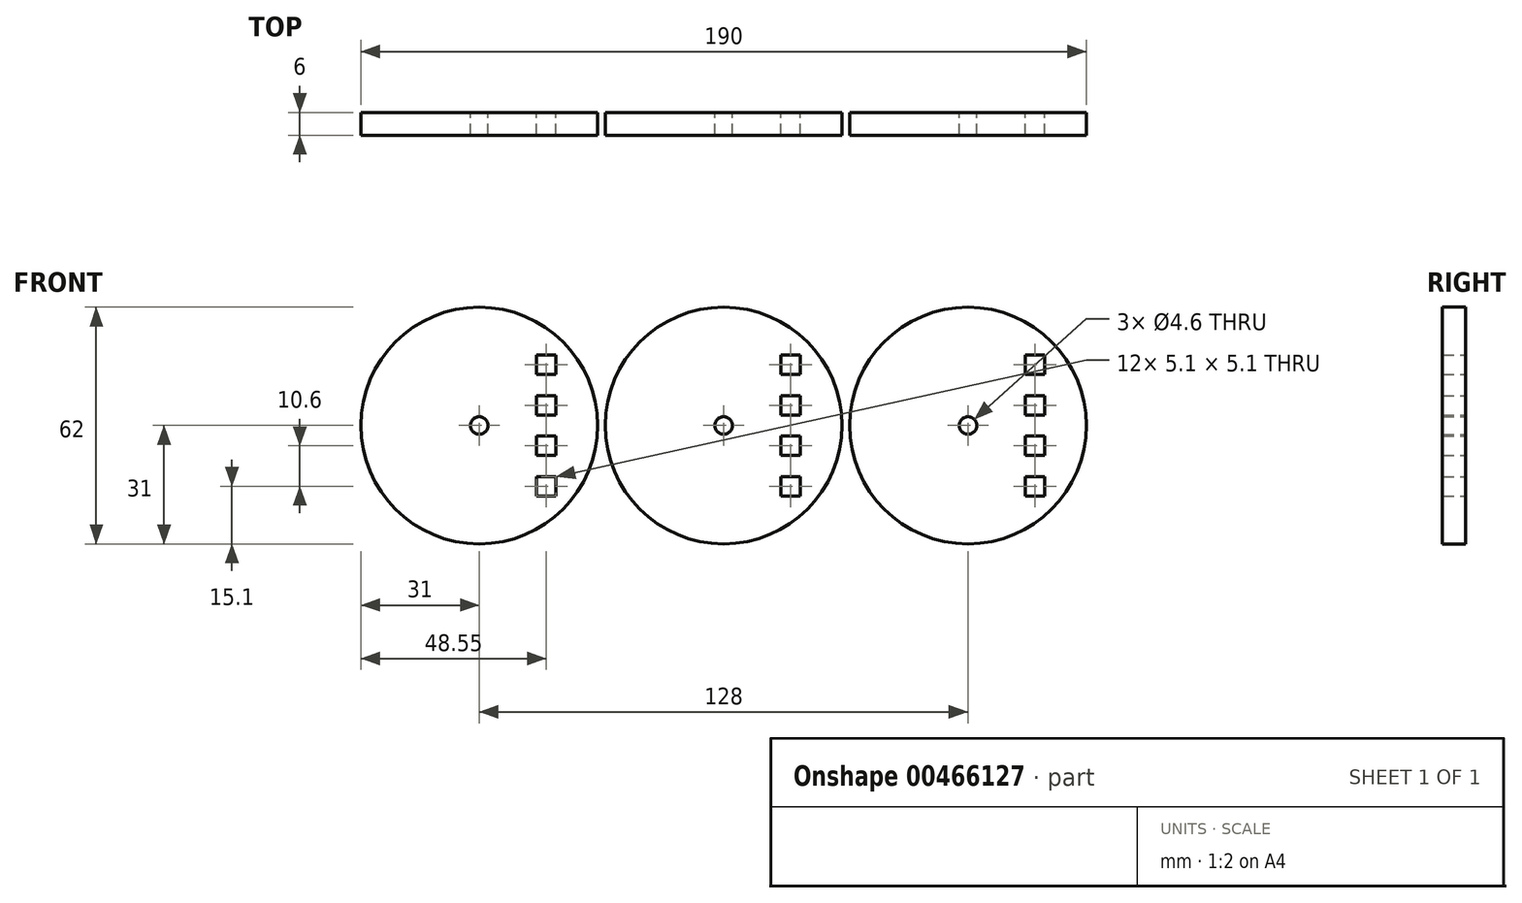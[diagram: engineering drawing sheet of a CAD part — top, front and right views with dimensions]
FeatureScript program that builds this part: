
annotation { "Feature Type Name" : "Feature", "Feature Type Description" : "" }
export const myFeature = defineFeature(function(context is Context, id is Id, definition is map)
    precondition{}
    {
        {
            var Q0;
            Q0=qCreatedBy(makeId("Front.planeOp"),FACE);
            var sketch = newSketch(context, id + "F0", { "sketchPlane" : qUnion([Q0])});
            skCircle(sketch, "E0", {"center": v(0, 0) * mm, "radius": 31 * mm});
            skLineSegment(sketch, "E1.bottom", {"start": v(15, 18.45) * mm, "end": v(20.1, 18.45) * mm});
            skLineSegment(sketch, "E1.top", {"start": v(15, 13.35) * mm, "end": v(20.1, 13.35) * mm});
            skLineSegment(sketch, "E1.left", {"start": v(15, 18.45) * mm, "end": v(15, 13.35) * mm});
            skLineSegment(sketch, "E1.right", {"start": v(20.1, 18.45) * mm, "end": v(20.1, 13.35) * mm});
            skLineSegment(sketch, "E2.bottom", {"start": v(15, 7.85) * mm, "end": v(20.1, 7.85) * mm});
            skLineSegment(sketch, "E2.top", {"start": v(15, 2.75) * mm, "end": v(20.1, 2.75) * mm});
            skLineSegment(sketch, "E2.left", {"start": v(15, 7.85) * mm, "end": v(15, 2.75) * mm});
            skLineSegment(sketch, "E2.right", {"start": v(20.1, 7.85) * mm, "end": v(20.1, 2.75) * mm});
            skLineSegment(sketch, "E3.bottom", {"start": v(15, -2.75) * mm, "end": v(20.1, -2.75) * mm});
            skLineSegment(sketch, "E3.top", {"start": v(15, -7.85) * mm, "end": v(20.1, -7.85) * mm});
            skLineSegment(sketch, "E3.left", {"start": v(15, -2.75) * mm, "end": v(15, -7.85) * mm});
            skLineSegment(sketch, "E3.right", {"start": v(20.1, -2.75) * mm, "end": v(20.1, -7.85) * mm});
            skLineSegment(sketch, "E4.bottom", {"start": v(15, -13.35) * mm, "end": v(20.1, -13.35) * mm});
            skLineSegment(sketch, "E4.top", {"start": v(15, -18.45) * mm, "end": v(20.1, -18.45) * mm});
            skLineSegment(sketch, "E4.left", {"start": v(15, -13.35) * mm, "end": v(15, -18.45) * mm});
            skLineSegment(sketch, "E4.right", {"start": v(20.1, -13.35) * mm, "end": v(20.1, -18.45) * mm});
            skCircle(sketch, "E5", {"center": v(0, 0) * mm, "radius": 2.3 * mm});
            skCircle(sketch, "E6.1.0.0", {"center": v(64, 0) * mm, "radius": 2.3 * mm});
            skCircle(sketch, "E6.1.0.1", {"center": v(64, 0) * mm, "radius": 31 * mm});
            skLineSegment(sketch, "E6.1.0.2", {"start": v(79, 18.45) * mm, "end": v(79, 13.35) * mm});
            skLineSegment(sketch, "E6.1.0.3", {"start": v(84.1, -2.75) * mm, "end": v(84.1, -7.85) * mm});
            skLineSegment(sketch, "E6.1.0.4", {"start": v(79, 7.85) * mm, "end": v(84.1, 7.85) * mm});
            skLineSegment(sketch, "E6.1.0.5", {"start": v(79, 2.75) * mm, "end": v(84.1, 2.75) * mm});
            skLineSegment(sketch, "E6.1.0.6", {"start": v(84.1, 7.85) * mm, "end": v(84.1, 2.75) * mm});
            skLineSegment(sketch, "E6.1.0.7", {"start": v(79, -18.45) * mm, "end": v(84.1, -18.45) * mm});
            skLineSegment(sketch, "E6.1.0.8", {"start": v(84.1, -13.35) * mm, "end": v(84.1, -18.45) * mm});
            skLineSegment(sketch, "E6.1.0.9", {"start": v(79, -2.75) * mm, "end": v(84.1, -2.75) * mm});
            skLineSegment(sketch, "E6.1.0.10", {"start": v(79, 13.35) * mm, "end": v(84.1, 13.35) * mm});
            skLineSegment(sketch, "E6.1.0.11", {"start": v(79, -13.35) * mm, "end": v(84.1, -13.35) * mm});
            skLineSegment(sketch, "E6.1.0.12", {"start": v(84.1, 18.45) * mm, "end": v(84.1, 13.35) * mm});
            skLineSegment(sketch, "E6.1.0.13", {"start": v(79, 7.85) * mm, "end": v(79, 2.75) * mm});
            skLineSegment(sketch, "E6.1.0.14", {"start": v(79, -7.85) * mm, "end": v(84.1, -7.85) * mm});
            skLineSegment(sketch, "E6.1.0.15", {"start": v(79, 18.45) * mm, "end": v(84.1, 18.45) * mm});
            skLineSegment(sketch, "E6.1.0.16", {"start": v(79, -13.35) * mm, "end": v(79, -18.45) * mm});
            skLineSegment(sketch, "E6.1.0.17", {"start": v(79, -2.75) * mm, "end": v(79, -7.85) * mm});
            skCircle(sketch, "E6.2.0.0", {"center": v(128, 0) * mm, "radius": 2.3 * mm});
            skCircle(sketch, "E6.2.0.1", {"center": v(128, 0) * mm, "radius": 31 * mm});
            skLineSegment(sketch, "E6.2.0.2", {"start": v(143, 18.45) * mm, "end": v(143, 13.35) * mm});
            skLineSegment(sketch, "E6.2.0.3", {"start": v(148.1, -2.75) * mm, "end": v(148.1, -7.85) * mm});
            skLineSegment(sketch, "E6.2.0.4", {"start": v(143, 7.85) * mm, "end": v(148.1, 7.85) * mm});
            skLineSegment(sketch, "E6.2.0.5", {"start": v(143, 2.75) * mm, "end": v(148.1, 2.75) * mm});
            skLineSegment(sketch, "E6.2.0.6", {"start": v(148.1, 7.85) * mm, "end": v(148.1, 2.75) * mm});
            skLineSegment(sketch, "E6.2.0.7", {"start": v(143, -18.45) * mm, "end": v(148.1, -18.45) * mm});
            skLineSegment(sketch, "E6.2.0.8", {"start": v(148.1, -13.35) * mm, "end": v(148.1, -18.45) * mm});
            skLineSegment(sketch, "E6.2.0.9", {"start": v(143, -2.75) * mm, "end": v(148.1, -2.75) * mm});
            skLineSegment(sketch, "E6.2.0.10", {"start": v(143, 13.35) * mm, "end": v(148.1, 13.35) * mm});
            skLineSegment(sketch, "E6.2.0.11", {"start": v(143, -13.35) * mm, "end": v(148.1, -13.35) * mm});
            skLineSegment(sketch, "E6.2.0.12", {"start": v(148.1, 18.45) * mm, "end": v(148.1, 13.35) * mm});
            skLineSegment(sketch, "E6.2.0.13", {"start": v(143, 7.85) * mm, "end": v(143, 2.75) * mm});
            skLineSegment(sketch, "E6.2.0.14", {"start": v(143, -7.85) * mm, "end": v(148.1, -7.85) * mm});
            skLineSegment(sketch, "E6.2.0.15", {"start": v(143, 18.45) * mm, "end": v(148.1, 18.45) * mm});
            skLineSegment(sketch, "E6.2.0.16", {"start": v(143, -13.35) * mm, "end": v(143, -18.45) * mm});
            skLineSegment(sketch, "E6.2.0.17", {"start": v(143, -2.75) * mm, "end": v(143, -7.85) * mm});
            skLineSegment(sketch, "E6.direction1", {"start": v(15, -18.45) * mm, "end": v(79, -18.45) * mm, "construction": true});
            skSolve(sketch);
        }
        {
            var Q0;
            Q0 = qSketchRegion(id + "F0", true);
            extrude(context, id + "F1", {"entities" : qUnion([Q0]), "depth" : 6 * mm});
        }
    });
